# Revit family: 17. Wichmann Kabelbox UFK EF_WAND
name_source: partatom
category: HLS-Bauteile
revit_build: Autodesk Revit 2018 (Build: 20170223_1515(x64)
units: mm (PartAtom-declared; Revit-internal decimal feet)

## family parameters
Basisbauteil = Wand
Beim Laden mit Abzugskörper schneiden = Nein
Bemaßung runder Anschluss = Durchmesser verwenden
Gemeinsam genutzt = Nein
Immer vertikal = Ja
Raumberechnungspunkt = Nein
Teiletyp = Normal

## types (70) — shared parameters
Rohbauöffnung = Ja
Tbox = 270 mm  [stored 0.885827 ft]
zero-valued in all types: HO

## per-type parameters (varying)
| type | BA | BI | BR | HA | HAN | HI | HR |
| Kabelbox UFK EF, 110x335x270 mm | 335 mm  [stored 1.09908 ft] | 305 mm  [stored 1.00066 ft] | 375 mm  [stored 1.23031 ft] | 110 mm  [stored 0.360892 ft] | EFUFK7530 | 75 mm  [stored 0.246063 ft] | 125 mm  [stored 0.410105 ft] |
| Kabelbox UFK EF, 110x280x270 mm | 280 mm  [stored 0.918635 ft] | 250 mm  [stored 0.82021 ft] | 320 mm  [stored 1.04987 ft] | 110 mm  [stored 0.360892 ft] | EFUFK7525 | 75 mm  [stored 0.246063 ft] | 125 mm  [stored 0.410105 ft] |
| Kabelbox UFK EF, 110x230x270 mm | 230 mm  [stored 0.754593 ft] | 200 mm  [stored 0.656168 ft] | 270 mm  [stored 0.885827 ft] | 110 mm  [stored 0.360892 ft] | EFUFK7520 | 75 mm  [stored 0.246063 ft] | 125 mm  [stored 0.410105 ft] |
| Kabelbox UFK EF, 110x220x270 mm | 220 mm  [stored 0.721785 ft] | 190 mm | 260 mm  [stored 0.853018 ft] | 110 mm  [stored 0.360892 ft] | EFUFK7519 | 75 mm  [stored 0.246063 ft] | 125 mm  [stored 0.410105 ft] |
| Kabelbox UFK EF, 110x200x270 mm | 200 mm  [stored 0.656168 ft] | 170 mm  [stored 0.557743 ft] | 240 mm  [stored 0.787402 ft] | 110 mm  [stored 0.360892 ft] | EFUFK7517 | 75 mm  [stored 0.246063 ft] | 125 mm  [stored 0.410105 ft] |
| Kabelbox UFK EF, 110x120x270 mm | 120 mm  [stored 0.393701 ft] | 90 mm  [stored 0.295276 ft] | 160 mm  [stored 0.524934 ft] | 110 mm  [stored 0.360892 ft] | EFUFK759 | 75 mm  [stored 0.246063 ft] | 125 mm  [stored 0.410105 ft] |
| Kabelbox UFK EF, 100x535x270 mm | 535 mm | 505 mm | 575 mm | 100 mm  [stored 0.328084 ft] | EFUFK6650 | 66 mm  [stored 0.216535 ft] | 115 mm  [stored 0.377297 ft] |
| Kabelbox UFK EF, 100x460x270 mm | 460 mm | 430 mm | 500 mm | 100 mm  [stored 0.328084 ft] | EFUFK6643 | 66 mm  [stored 0.216535 ft] | 115 mm  [stored 0.377297 ft] |
| Kabelbox UFK EF, 100x435x270 mm | 435 mm | 405 mm | 475 mm | 100 mm  [stored 0.328084 ft] | EFUFK6640 | 66 mm  [stored 0.216535 ft] | 115 mm  [stored 0.377297 ft] |
| Kabelbox UFK EF, 100x335x270 mm | 335 mm  [stored 1.09908 ft] | 305 mm  [stored 1.00066 ft] | 375 mm  [stored 1.23031 ft] | 100 mm  [stored 0.328084 ft] | EFUFK6630 | 66 mm  [stored 0.216535 ft] | 115 mm  [stored 0.377297 ft] |
| Kabelbox UFK EF, 100x280x270 mm | 280 mm  [stored 0.918635 ft] | 250 mm  [stored 0.82021 ft] | 320 mm  [stored 1.04987 ft] | 100 mm  [stored 0.328084 ft] | EFUFK6625 | 66 mm  [stored 0.216535 ft] | 115 mm  [stored 0.377297 ft] |
| Kabelbox UFK EF, 100x230x270 mm | 230 mm  [stored 0.754593 ft] | 200 mm  [stored 0.656168 ft] | 270 mm  [stored 0.885827 ft] | 100 mm  [stored 0.328084 ft] | EFUFK6620 | 66 mm  [stored 0.216535 ft] | 115 mm  [stored 0.377297 ft] |
| Kabelbox UFK EF, 100x220x270 mm | 220 mm  [stored 0.721785 ft] | 190 mm | 260 mm  [stored 0.853018 ft] | 100 mm  [stored 0.328084 ft] | EFUFK6619 | 66 mm  [stored 0.216535 ft] | 115 mm  [stored 0.377297 ft] |
| Kabelbox UFK EF, 100x200x270 mm | 200 mm  [stored 0.656168 ft] | 170 mm  [stored 0.557743 ft] | 240 mm  [stored 0.787402 ft] | 100 mm  [stored 0.328084 ft] | EFUFK6617 | 66 mm  [stored 0.216535 ft] | 115 mm  [stored 0.377297 ft] |
| Kabelbox UFK EF, 100x120x270 mm | 120 mm  [stored 0.393701 ft] | 90 mm  [stored 0.295276 ft] | 160 mm  [stored 0.524934 ft] | 100 mm  [stored 0.328084 ft] | EFUFK669 | 66 mm  [stored 0.216535 ft] | 115 mm  [stored 0.377297 ft] |
| Kabelbox UFK EF, 90x535x270 mm | 535 mm | 505 mm | 575 mm | 90 mm  [stored 0.295276 ft] | EFUFK5850 | 58 mm  [stored 0.190289 ft] | 105 mm  [stored 0.344488 ft] |
| Kabelbox UFK EF, 90x460x270 mm | 460 mm | 430 mm | 500 mm | 90 mm  [stored 0.295276 ft] | EFUFK5843 | 58 mm  [stored 0.190289 ft] | 105 mm  [stored 0.344488 ft] |
| Kabelbox UFK EF, 90x435x270 mm | 435 mm | 405 mm | 475 mm | 90 mm  [stored 0.295276 ft] | EFUFK5840 | 58 mm  [stored 0.190289 ft] | 105 mm  [stored 0.344488 ft] |
| Kabelbox UFK EF, 90x380x270 mm | 380 mm | 350 mm  [stored 1.14829 ft] | 420 mm | 90 mm  [stored 0.295276 ft] | EFUFK5835 | 58 mm  [stored 0.190289 ft] | 105 mm  [stored 0.344488 ft] |
| Kabelbox UFK EF, 90x280x270 mm | 280 mm  [stored 0.918635 ft] | 250 mm  [stored 0.82021 ft] | 320 mm  [stored 1.04987 ft] | 90 mm  [stored 0.295276 ft] | EFUFK5825 | 58 mm  [stored 0.190289 ft] | 105 mm  [stored 0.344488 ft] |
| Kabelbox UFK EF, 90x230x270 mm | 230 mm  [stored 0.754593 ft] | 200 mm  [stored 0.656168 ft] | 270 mm  [stored 0.885827 ft] | 90 mm  [stored 0.295276 ft] | EFUFK5820 | 58 mm  [stored 0.190289 ft] | 105 mm  [stored 0.344488 ft] |
| Kabelbox UFK EF, 90x220x270 mm | 220 mm  [stored 0.721785 ft] | 190 mm | 260 mm  [stored 0.853018 ft] | 90 mm  [stored 0.295276 ft] | EFUFK5819 | 58 mm  [stored 0.190289 ft] | 105 mm  [stored 0.344488 ft] |
| Kabelbox UFK EF, 90x200x270 mm | 200 mm  [stored 0.656168 ft] | 170 mm  [stored 0.557743 ft] | 240 mm  [stored 0.787402 ft] | 90 mm  [stored 0.295276 ft] | EFUFK5817 | 58 mm  [stored 0.190289 ft] | 105 mm  [stored 0.344488 ft] |
| Kabelbox UFK EF, 90x120x270 mm | 120 mm  [stored 0.393701 ft] | 90 mm  [stored 0.295276 ft] | 160 mm  [stored 0.524934 ft] | 90 mm  [stored 0.295276 ft] | EFUFK589 | 58 mm  [stored 0.190289 ft] | 105 mm  [stored 0.344488 ft] |
| Kabelbox UFK EF, 80x535x270 mm | 535 mm | 505 mm | 575 mm | 80 mm  [stored 0.262467 ft] | EFUFK5250 | 52 mm | 95 mm |
| Kabelbox UFK EF, 80x460x270 mm | 460 mm | 430 mm | 500 mm | 80 mm  [stored 0.262467 ft] | EFUFK5243 | 52 mm | 95 mm |
| Kabelbox UFK EF, 80x435x270 mm | 435 mm | 405 mm | 475 mm | 80 mm  [stored 0.262467 ft] | EFUFK5240 | 52 mm | 95 mm |
| Kabelbox UFK EF, 80x380x270 mm | 380 mm | 350 mm  [stored 1.14829 ft] | 420 mm | 80 mm  [stored 0.262467 ft] | EFUFK5235 | 52 mm | 95 mm |
| Kabelbox UFK EF, 80x335x270 mm | 335 mm  [stored 1.09908 ft] | 305 mm  [stored 1.00066 ft] | 375 mm  [stored 1.23031 ft] | 80 mm  [stored 0.262467 ft] | EFUFK5230 | 52 mm | 95 mm |
| Kabelbox UFK EF, 80x230x270 mm | 230 mm  [stored 0.754593 ft] | 200 mm  [stored 0.656168 ft] | 270 mm  [stored 0.885827 ft] | 80 mm  [stored 0.262467 ft] | EFUFK5220 | 52 mm | 95 mm |
| Kabelbox UFK EF, 80x220x270 mm | 220 mm  [stored 0.721785 ft] | 190 mm | 260 mm  [stored 0.853018 ft] | 80 mm  [stored 0.262467 ft] | EFUFK5219 | 52 mm | 95 mm |
| Kabelbox UFK EF, 80x200x270 mm | 200 mm  [stored 0.656168 ft] | 170 mm  [stored 0.557743 ft] | 240 mm  [stored 0.787402 ft] | 80 mm  [stored 0.262467 ft] | EFUFK5217 | 52 mm | 95 mm |
| Kabelbox UFK EF, 80x120x270 mm | 120 mm  [stored 0.393701 ft] | 90 mm  [stored 0.295276 ft] | 160 mm  [stored 0.524934 ft] | 80 mm  [stored 0.262467 ft] | EFUFK529 | 52 mm | 95 mm |
| Kabelbox UFK EF, 68x535x270 mm | 535 mm | 505 mm | 575 mm | 68 mm | EFUFK4850 | 48 mm  [stored 0.15748 ft] | 83 mm  [stored 0.27231 ft] |
| Kabelbox UFK EF, 68x460x270 mm | 460 mm | 430 mm | 500 mm | 68 mm | EFUFK4843 | 48 mm  [stored 0.15748 ft] | 83 mm  [stored 0.27231 ft] |
| Kabelbox UFK EF, 68x435x270 mm | 435 mm | 405 mm | 475 mm | 68 mm | EFUFK4840 | 48 mm  [stored 0.15748 ft] | 83 mm  [stored 0.27231 ft] |
| Kabelbox UFK EF, 68x380x270 mm | 380 mm | 350 mm  [stored 1.14829 ft] | 420 mm | 68 mm | EFUFK4835 | 48 mm  [stored 0.15748 ft] | 83 mm  [stored 0.27231 ft] |
| Kabelbox UFK EF, 68x335x270 mm | 335 mm  [stored 1.09908 ft] | 305 mm  [stored 1.00066 ft] | 375 mm  [stored 1.23031 ft] | 68 mm | EFUFK4830 | 48 mm  [stored 0.15748 ft] | 83 mm  [stored 0.27231 ft] |
| Kabelbox UFK EF, 68x280x270 mm | 280 mm  [stored 0.918635 ft] | 250 mm  [stored 0.82021 ft] | 320 mm  [stored 1.04987 ft] | 68 mm | EFUFK4825 | 48 mm  [stored 0.15748 ft] | 83 mm  [stored 0.27231 ft] |
| Kabelbox UFK EF, 68x220x270 mm | 220 mm  [stored 0.721785 ft] | 190 mm | 260 mm  [stored 0.853018 ft] | 68 mm | EFUFK4819 | 48 mm  [stored 0.15748 ft] | 83 mm  [stored 0.27231 ft] |
| Kabelbox UFK EF, 68x200x270 mm | 200 mm  [stored 0.656168 ft] | 170 mm  [stored 0.557743 ft] | 240 mm  [stored 0.787402 ft] | 68 mm | EFUFK4817 | 48 mm  [stored 0.15748 ft] | 83 mm  [stored 0.27231 ft] |
| Kabelbox UFK EF, 68x120x270 mm | 120 mm  [stored 0.393701 ft] | 90 mm  [stored 0.295276 ft] | 160 mm  [stored 0.524934 ft] | 68 mm | EFUFK489 | 48 mm  [stored 0.15748 ft] | 83 mm  [stored 0.27231 ft] |
| Kabelbox UFK EF, 55x535x270 mm | 535 mm | 505 mm | 575 mm | 55 mm  [stored 0.180446 ft] | EFUFK3850 | 38 mm  [stored 0.124672 ft] | 70 mm  [stored 0.229659 ft] |
| Kabelbox UFK EF, 55x460x270 mm | 460 mm | 430 mm | 500 mm | 55 mm  [stored 0.180446 ft] | EFUFK3843 | 38 mm  [stored 0.124672 ft] | 70 mm  [stored 0.229659 ft] |
| Kabelbox UFK EF, 55x435x270 mm | 435 mm | 405 mm | 475 mm | 55 mm  [stored 0.180446 ft] | EFUFK3840 | 38 mm  [stored 0.124672 ft] | 70 mm  [stored 0.229659 ft] |
| Kabelbox UFK EF, 55x380x270 mm | 380 mm | 350 mm  [stored 1.14829 ft] | 420 mm | 55 mm  [stored 0.180446 ft] | EFUFK3835 | 38 mm  [stored 0.124672 ft] | 70 mm  [stored 0.229659 ft] |
| Kabelbox UFK EF, 55x335x270 mm | 335 mm  [stored 1.09908 ft] | 305 mm  [stored 1.00066 ft] | 375 mm  [stored 1.23031 ft] | 55 mm  [stored 0.180446 ft] | EFUFK3830 | 38 mm  [stored 0.124672 ft] | 70 mm  [stored 0.229659 ft] |
| Kabelbox UFK EF, 55x280x270 mm | 280 mm  [stored 0.918635 ft] | 250 mm  [stored 0.82021 ft] | 320 mm  [stored 1.04987 ft] | 55 mm  [stored 0.180446 ft] | EFUFK3825 | 38 mm  [stored 0.124672 ft] | 70 mm  [stored 0.229659 ft] |
| Kabelbox UFK EF, 55x230x270 mm | 230 mm  [stored 0.754593 ft] | 200 mm  [stored 0.656168 ft] | 270 mm  [stored 0.885827 ft] | 55 mm  [stored 0.180446 ft] | EFUFK3820 | 38 mm  [stored 0.124672 ft] | 70 mm  [stored 0.229659 ft] |
| Kabelbox UFK EF, 55x200x270 mm | 200 mm  [stored 0.656168 ft] | 170 mm  [stored 0.557743 ft] | 240 mm  [stored 0.787402 ft] | 55 mm  [stored 0.180446 ft] | EFUFK3817 | 38 mm  [stored 0.124672 ft] | 70 mm  [stored 0.229659 ft] |
| Kabelbox UFK EF, 55x120x270 mm | 120 mm  [stored 0.393701 ft] | 90 mm  [stored 0.295276 ft] | 160 mm  [stored 0.524934 ft] | 55 mm  [stored 0.180446 ft] | EFUFK389 | 38 mm  [stored 0.124672 ft] | 70 mm  [stored 0.229659 ft] |
| Kabelbox UFK EF, 41x535x270 mm | 535 mm | 505 mm | 575 mm | 41 mm  [stored 0.134514 ft] | EFUFK2850 | 28 mm  [stored 0.0918635 ft] | 56 mm  [stored 0.183727 ft] |
| Kabelbox UFK EF, 41x460x270 mm | 460 mm | 430 mm | 500 mm | 41 mm  [stored 0.134514 ft] | EFUFK2843 | 28 mm  [stored 0.0918635 ft] | 56 mm  [stored 0.183727 ft] |
| Kabelbox UFK EF, 41x435x270 mm | 435 mm | 405 mm | 475 mm | 41 mm  [stored 0.134514 ft] | EFUFK2840 | 28 mm  [stored 0.0918635 ft] | 56 mm  [stored 0.183727 ft] |
| Kabelbox UFK EF, 41x380x270 mm | 380 mm | 350 mm  [stored 1.14829 ft] | 420 mm | 41 mm  [stored 0.134514 ft] | EFUFK2835 | 28 mm  [stored 0.0918635 ft] | 56 mm  [stored 0.183727 ft] |
| Kabelbox UFK EF, 41x335x270 mm | 335 mm  [stored 1.09908 ft] | 305 mm  [stored 1.00066 ft] | 375 mm  [stored 1.23031 ft] | 41 mm  [stored 0.134514 ft] | EFUFK2830 | 28 mm  [stored 0.0918635 ft] | 56 mm  [stored 0.183727 ft] |
| Kabelbox UFK EF, 41x280x270 mm | 280 mm  [stored 0.918635 ft] | 250 mm  [stored 0.82021 ft] | 320 mm  [stored 1.04987 ft] | 41 mm  [stored 0.134514 ft] | EFUFK2825 | 28 mm  [stored 0.0918635 ft] | 56 mm  [stored 0.183727 ft] |
| Kabelbox UFK EF, 41x230x270 mm | 230 mm  [stored 0.754593 ft] | 200 mm  [stored 0.656168 ft] | 270 mm  [stored 0.885827 ft] | 41 mm  [stored 0.134514 ft] | EFUFK2820 | 28 mm  [stored 0.0918635 ft] | 56 mm  [stored 0.183727 ft] |
| Kabelbox UFK EF, 41x220x270 mm | 220 mm  [stored 0.721785 ft] | 190 mm | 260 mm  [stored 0.853018 ft] | 41 mm  [stored 0.134514 ft] | EFUFK2819 | 28 mm  [stored 0.0918635 ft] | 56 mm  [stored 0.183727 ft] |
| Kabelbox UFK EF, 41x200x270 mm | 200 mm  [stored 0.656168 ft] | 170 mm  [stored 0.557743 ft] | 240 mm  [stored 0.787402 ft] | 41 mm  [stored 0.134514 ft] | EFUFK2817 | 28 mm  [stored 0.0918635 ft] | 56 mm  [stored 0.183727 ft] |
| Kabelbox UFK EF, 41x120x270 mm | 120 mm  [stored 0.393701 ft] | 90 mm  [stored 0.295276 ft] | 160 mm  [stored 0.524934 ft] | 41 mm  [stored 0.134514 ft] | EFUFK289 | 28 mm  [stored 0.0918635 ft] | 56 mm  [stored 0.183727 ft] |
| Kabelbox UFK EF, 110x460x270 mm | 460 mm | 430 mm | 500 mm | 110 mm  [stored 0.360892 ft] | EFUFK7543 | 75 mm  [stored 0.246063 ft] | 125 mm  [stored 0.410105 ft] |
| Kabelbox UFK EF, 110x435x270 mm | 435 mm | 405 mm | 475 mm | 110 mm  [stored 0.360892 ft] | EFUFK7540 | 75 mm  [stored 0.246063 ft] | 125 mm  [stored 0.410105 ft] |
| Kabelbox UFK EF, 110x380x270 mm | 380 mm | 350 mm  [stored 1.14829 ft] | 420 mm | 110 mm  [stored 0.360892 ft] | EFUFK7535 | 75 mm  [stored 0.246063 ft] | 125 mm  [stored 0.410105 ft] |
| Kabelbox UFK EF, 100x380x270 mm | 380 mm | 350 mm  [stored 1.14829 ft] | 420 mm | 100 mm  [stored 0.328084 ft] | EFUFK6635 | 66 mm  [stored 0.216535 ft] | 115 mm  [stored 0.377297 ft] |
| Kabelbox UFK EF, 90x335x270 mm | 335 mm  [stored 1.09908 ft] | 305 mm  [stored 1.00066 ft] | 375 mm  [stored 1.23031 ft] | 90 mm  [stored 0.295276 ft] | EFUFK5830 | 58 mm  [stored 0.190289 ft] | 105 mm  [stored 0.344488 ft] |
| Kabelbox UFK EF, 80x280x270 mm | 280 mm  [stored 0.918635 ft] | 250 mm  [stored 0.82021 ft] | 320 mm  [stored 1.04987 ft] | 80 mm  [stored 0.262467 ft] | EFUFK5225 | 52 mm | 95 mm |
| Kabelbox UFK EF, 68x230x270 mm | 230 mm  [stored 0.754593 ft] | 200 mm  [stored 0.656168 ft] | 270 mm  [stored 0.885827 ft] | 68 mm | EFUFK4820 | 48 mm  [stored 0.15748 ft] | 83 mm  [stored 0.27231 ft] |
| Kabelbox UFK EF, 55x220x270 mm | 220 mm  [stored 0.721785 ft] | 190 mm | 260 mm  [stored 0.853018 ft] | 55 mm  [stored 0.180446 ft] | EFUFK3819 | 38 mm  [stored 0.124672 ft] | 70 mm  [stored 0.229659 ft] |
| Kabelbox UFK EF, 110x535x270 mm | 535 mm | 505 mm | 575 mm | 110 mm  [stored 0.360892 ft] | EFUFK7550 | 75 mm  [stored 0.246063 ft] | 125 mm  [stored 0.410105 ft] |

note: [stored X ft] marks values corroborated as IEEE doubles in the binary element streams (Revit-internal decimal feet)
